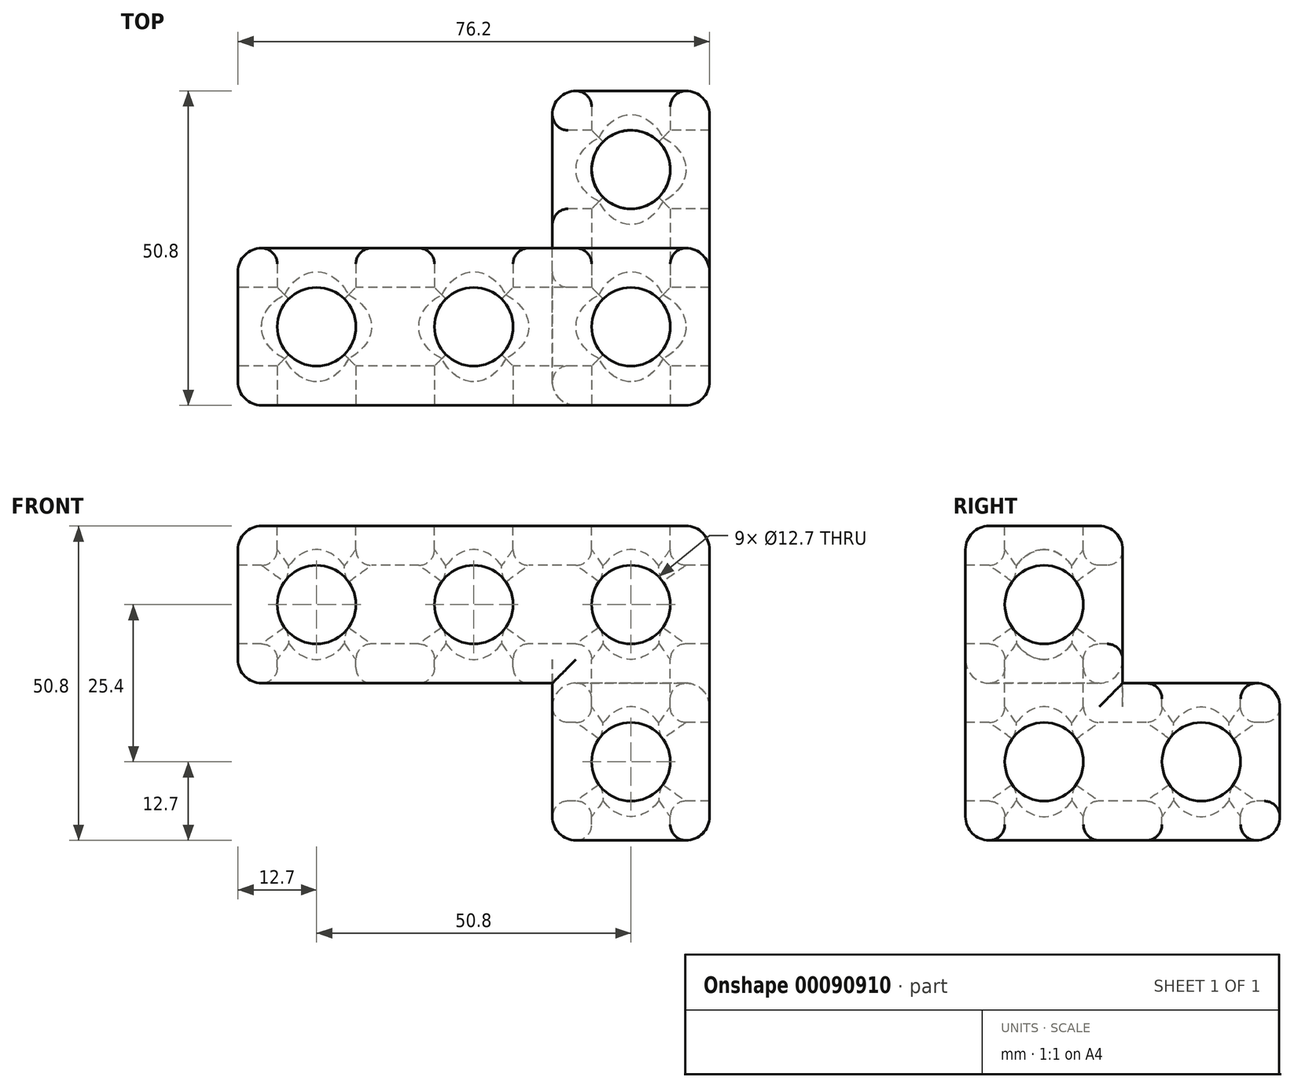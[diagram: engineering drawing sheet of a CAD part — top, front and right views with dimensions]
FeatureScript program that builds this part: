
annotation { "Feature Type Name" : "Feature", "Feature Type Description" : "" }
export const myFeature = defineFeature(function(context is Context, id is Id, definition is map)
    precondition{}
    {
        {
            var Q0;
            Q0=qCreatedBy(makeId("Top.planeOp"),FACE);
            var sketch = newSketch(context, id + "F0", { "sketchPlane" : qUnion([Q0])});
            skLineSegment(sketch, "E0.bottom", {"start": v(0, 0) * mm, "end": v(76.2, 0) * mm});
            skLineSegment(sketch, "E0.top", {"start": v(0, 25.4) * mm, "end": v(76.2, 25.4) * mm});
            skLineSegment(sketch, "E0.left", {"start": v(0, 0) * mm, "end": v(0, 25.4) * mm});
            skLineSegment(sketch, "E0.right", {"start": v(76.2, 0) * mm, "end": v(76.2, 25.4) * mm});
            skSolve(sketch);
        }
        {
            var Q0;
            Q0 = qSketchRegion(id + "F0", true);
            extrude(context, id + "F1", {"entities" : qUnion([Q0]), "depth" : 25.4 * mm});
        }
        {
            var Q0;
            Q0=makeQuery(id+"F1.opExtrude","CAP_FACE",FACE,{"disambiguationData":[OSD([sQuery(id+"F0.wireOp",EDGE,"E0.bottom"),sQuery(id+"F0.wireOp",EDGE,"E0.top"),sQuery(id+"F0.wireOp",EDGE,"E0.left"),sQuery(id+"F0.wireOp",EDGE,"E0.right")])],"isStart":true});
            var sketch = newSketch(context, id + "F2", { "sketchPlane" : qUnion([Q0])});
            skLineSegment(sketch, "E1.bottom", {"start": v(76.2, 0) * mm, "end": v(50.8, 0) * mm});
            skLineSegment(sketch, "E1.top", {"start": v(76.2, -50.8) * mm, "end": v(50.8, -50.8) * mm});
            skLineSegment(sketch, "E1.left", {"start": v(76.2, 0) * mm, "end": v(76.2, -50.8) * mm});
            skLineSegment(sketch, "E1.right", {"start": v(50.8, 0) * mm, "end": v(50.8, -50.8) * mm});
            skSolve(sketch);
        }
        {
            var Q0;
            Q0 = qSketchRegion(id + "F2", true);
            extrude(context, id + "F3", {"entities" : qUnion([Q0]), "operationType" : NewBodyOperationType.ADD, "depth" : 25.4 * mm});
        }
        {
            var Q0;
            Q0=makeQuery(id+"F1.opExtrude","CAP_FACE",FACE,{"disambiguationData":[OSD([sQuery(id+"F0.wireOp",EDGE,"E0.bottom"),sQuery(id+"F0.wireOp",EDGE,"E0.top"),sQuery(id+"F0.wireOp",EDGE,"E0.left"),sQuery(id+"F0.wireOp",EDGE,"E0.right")])],"isStart":false});
            var sketch = newSketch(context, id + "F4", { "sketchPlane" : qUnion([Q0])});
            skCircle(sketch, "E2", {"center": v(12.7, 12.7) * mm, "radius": 6.35 * mm});
            skCircle(sketch, "E3.0.1.0", {"center": v(12.7, 38.1) * mm, "radius": 6.35 * mm});
            skCircle(sketch, "E3.1.0.0", {"center": v(38.1, 12.7) * mm, "radius": 6.35 * mm});
            skCircle(sketch, "E3.1.1.0", {"center": v(38.1, 38.1) * mm, "radius": 6.35 * mm});
            skCircle(sketch, "E3.2.0.0", {"center": v(63.5, 12.7) * mm, "radius": 6.35 * mm});
            skCircle(sketch, "E3.2.1.0", {"center": v(63.5, 38.1) * mm, "radius": 6.35 * mm});
            skLineSegment(sketch, "E3.direction1", {"start": v(12.7, 12.7) * mm, "end": v(38.1, 12.7) * mm, "construction": true});
            skLineSegment(sketch, "E3.direction2", {"start": v(12.7, 12.7) * mm, "end": v(12.7, 38.1) * mm, "construction": true});
            skSolve(sketch);
        }
        {
            var Q0;
            Q0 = qSketchRegion(id + "F4", true);
            extrude(context, id + "F5", {"entities" : qUnion([Q0]), "operationType" : NewBodyOperationType.REMOVE, "oppositeDirection" : true, "depth" : 76.2 * mm});
        }
        {
            var Q0;
            Q0=makeQuery(id+"F3.boolean.opBoolean","MERGE",FACE,{"derivedFrom":[makeQuery(id+"F1.opExtrude","SWEPT_FACE",FACE,{"disambiguationData":[OSD([sQuery(id+"F0.wireOp",EDGE,"E0.bottom")])]}),makeQuery(id+"F3.opExtrude","SWEPT_FACE",FACE,{"disambiguationData":[OSD([sQuery(id+"F2.wireOp",EDGE,"E1.bottom")])]})]});
            var sketch = newSketch(context, id + "F6", { "sketchPlane" : qUnion([Q0])});
            skCircle(sketch, "E4", {"center": v(12.7, 12.7) * mm, "radius": 6.35 * mm});
            skCircle(sketch, "E5.0.1.0", {"center": v(12.7, -12.7) * mm, "radius": 6.35 * mm});
            skCircle(sketch, "E5.1.0.0", {"center": v(38.1, 12.7) * mm, "radius": 6.35 * mm});
            skCircle(sketch, "E5.1.1.0", {"center": v(38.1, -12.7) * mm, "radius": 6.35 * mm});
            skCircle(sketch, "E5.2.0.0", {"center": v(63.5, 12.7) * mm, "radius": 6.35 * mm});
            skCircle(sketch, "E5.2.1.0", {"center": v(63.5, -12.7) * mm, "radius": 6.35 * mm});
            skLineSegment(sketch, "E5.direction1", {"start": v(12.7, 12.7) * mm, "end": v(38.1, 12.7) * mm, "construction": true});
            skLineSegment(sketch, "E5.direction2", {"start": v(12.7, 12.7) * mm, "end": v(12.7, -12.7) * mm, "construction": true});
            skSolve(sketch);
        }
        {
            var Q0;
            Q0 = qSketchRegion(id + "F6", true);
            extrude(context, id + "F7", {"entities" : qUnion([Q0]), "operationType" : NewBodyOperationType.REMOVE, "oppositeDirection" : true, "depth" : 76.2 * mm});
        }
        {
            var Q0;
            Q0=makeQuery(id+"F1.opExtrude","SWEPT_FACE",FACE,{"disambiguationData":[OSD([sQuery(id+"F0.wireOp",EDGE,"E0.left")])]});
            var sketch = newSketch(context, id + "F8", { "sketchPlane" : qUnion([Q0])});
            skCircle(sketch, "E6", {"center": v(-12.7, 12.7) * mm, "radius": 6.35 * mm});
            skCircle(sketch, "E7.0.1.0", {"center": v(-12.7, -12.7) * mm, "radius": 6.35 * mm});
            skCircle(sketch, "E7.1.0.0", {"center": v(-38.1, 12.7) * mm, "radius": 6.35 * mm});
            skCircle(sketch, "E7.1.1.0", {"center": v(-38.1, -12.7) * mm, "radius": 6.35 * mm});
            skLineSegment(sketch, "E7.direction1", {"start": v(-12.7, 12.7) * mm, "end": v(-38.1, 12.7) * mm, "construction": true});
            skLineSegment(sketch, "E7.direction2", {"start": v(-12.7, 12.7) * mm, "end": v(-12.7, -12.7) * mm, "construction": true});
            skSolve(sketch);
        }
        {
            var Q0;
            Q0 = qSketchRegion(id + "F8", true);
            extrude(context, id + "F9", {"entities" : qUnion([Q0]), "operationType" : NewBodyOperationType.REMOVE, "oppositeDirection" : true, "depth" : 76.2 * mm});
        }
        {
            var Q0;
            Q0=makeQuery(id+"F5.boolean.opBoolean","COPY",EDGE,{"derivedFrom":makeQuery(id+"F5.opExtrude","CAP_EDGE",EDGE,{"disambiguationData":[OSD([sQuery(id+"F4.wireOp",EDGE,"E2")])],"isStart":true})});
            var Q1;
            Q1=makeQuery(id+"F5.boolean.opBoolean","COPY",EDGE,{"derivedFrom":makeQuery(id+"F5.opExtrude","CAP_EDGE",EDGE,{"disambiguationData":[OSD([sQuery(id+"F4.wireOp",EDGE,"E3.1.0.0")])],"isStart":true})});
            var Q2;
            Q2=makeQuery(id+"F5.boolean.opBoolean","COPY",EDGE,{"derivedFrom":makeQuery(id+"F5.opExtrude","CAP_EDGE",EDGE,{"disambiguationData":[OSD([sQuery(id+"F4.wireOp",EDGE,"E3.2.0.0")])],"isStart":true})});
            var Q3;
            Q3=makeQuery(id+"F7.boolean.opBoolean","COPY",EDGE,{"derivedFrom":makeQuery(id+"F7.opExtrude","CAP_EDGE",EDGE,{"disambiguationData":[OSD([sQuery(id+"F6.wireOp",EDGE,"E4")])],"isStart":true})});
            var Q4;
            Q4=makeQuery(id+"F5.boolean.opBoolean","INTERSECT",EDGE,{"derivedFrom":[makeQuery(id+"F3.opExtrude","CAP_FACE",FACE,{"disambiguationData":[OSD([sQuery(id+"F2.wireOp",EDGE,"E1.bottom"),sQuery(id+"F2.wireOp",EDGE,"E1.top"),sQuery(id+"F2.wireOp",EDGE,"E1.left"),sQuery(id+"F2.wireOp",EDGE,"E1.right")])],"isStart":true}),makeQuery(id+"F5.opExtrude","SWEPT_FACE",FACE,{"disambiguationData":[OSD([sQuery(id+"F4.wireOp",EDGE,"E3.2.1.0")])]})]});
            var Q5;
            Q5=makeQuery(id+"F7.boolean.opBoolean","COPY",EDGE,{"derivedFrom":makeQuery(id+"F7.opExtrude","CAP_EDGE",EDGE,{"disambiguationData":[OSD([sQuery(id+"F6.wireOp",EDGE,"E5.1.0.0")])],"isStart":true})});
            var Q6;
            Q6=makeQuery(id+"F7.boolean.opBoolean","COPY",EDGE,{"derivedFrom":makeQuery(id+"F7.opExtrude","CAP_EDGE",EDGE,{"disambiguationData":[OSD([sQuery(id+"F6.wireOp",EDGE,"E5.2.0.0")])],"isStart":true})});
            var Q7;
            Q7=makeQuery(id+"F7.boolean.opBoolean","COPY",EDGE,{"derivedFrom":makeQuery(id+"F7.opExtrude","CAP_EDGE",EDGE,{"disambiguationData":[OSD([sQuery(id+"F6.wireOp",EDGE,"E5.2.1.0")])],"isStart":true})});
            var Q8;
            Q8=makeQuery(id+"F9.boolean.opBoolean","COPY",EDGE,{"derivedFrom":makeQuery(id+"F9.opExtrude","CAP_EDGE",EDGE,{"disambiguationData":[OSD([sQuery(id+"F8.wireOp",EDGE,"E7.0.1.0")])],"isStart":false})});
            var Q9;
            Q9=makeQuery(id+"F9.boolean.opBoolean","COPY",EDGE,{"derivedFrom":makeQuery(id+"F9.opExtrude","CAP_EDGE",EDGE,{"disambiguationData":[OSD([sQuery(id+"F8.wireOp",EDGE,"E7.1.1.0")])],"isStart":false})});
            var Q10;
            Q10=makeQuery(id+"F9.boolean.opBoolean","COPY",EDGE,{"derivedFrom":makeQuery(id+"F9.opExtrude","CAP_EDGE",EDGE,{"disambiguationData":[OSD([sQuery(id+"F8.wireOp",EDGE,"E6")])],"isStart":false})});
            var Q11;
            Q11=makeQuery(id+"F7.boolean.opBoolean","INTERSECT",EDGE,{"derivedFrom":[makeQuery(id+"F3.opExtrude","SWEPT_FACE",FACE,{"disambiguationData":[OSD([sQuery(id+"F2.wireOp",EDGE,"E1.top")])]}),makeQuery(id+"F7.opExtrude","SWEPT_FACE",FACE,{"disambiguationData":[OSD([sQuery(id+"F6.wireOp",EDGE,"E5.2.1.0")])]})]});
            var Q12;
            Q12=makeQuery(id+"F7.boolean.opBoolean","INTERSECT",EDGE,{"derivedFrom":[makeQuery(id+"F1.opExtrude","SWEPT_FACE",FACE,{"disambiguationData":[OSD([sQuery(id+"F0.wireOp",EDGE,"E0.top")])]}),makeQuery(id+"F7.opExtrude","SWEPT_FACE",FACE,{"disambiguationData":[OSD([sQuery(id+"F6.wireOp",EDGE,"E5.1.0.0")])]})]});
            var Q13;
            Q13=makeQuery(id+"F7.boolean.opBoolean","INTERSECT",EDGE,{"derivedFrom":[makeQuery(id+"F1.opExtrude","SWEPT_FACE",FACE,{"disambiguationData":[OSD([sQuery(id+"F0.wireOp",EDGE,"E0.top")])]}),makeQuery(id+"F7.opExtrude","SWEPT_FACE",FACE,{"disambiguationData":[OSD([sQuery(id+"F6.wireOp",EDGE,"E4")])]})]});
            var Q14;
            Q14=makeQuery(id+"F9.boolean.opBoolean","COPY",EDGE,{"derivedFrom":makeQuery(id+"F9.opExtrude","CAP_EDGE",EDGE,{"disambiguationData":[OSD([sQuery(id+"F8.wireOp",EDGE,"E6")])],"isStart":true})});
            var Q15;
            Q15=makeQuery(id+"F9.boolean.opBoolean","INTERSECT",EDGE,{"derivedFrom":[makeQuery(id+"F3.opExtrude","SWEPT_FACE",FACE,{"disambiguationData":[OSD([sQuery(id+"F2.wireOp",EDGE,"E1.right")])]}),makeQuery(id+"F9.opExtrude","SWEPT_FACE",FACE,{"disambiguationData":[OSD([sQuery(id+"F8.wireOp",EDGE,"E7.1.1.0")])]})]});
            var Q16;
            Q16=makeQuery(id+"F9.boolean.opBoolean","INTERSECT",EDGE,{"derivedFrom":[makeQuery(id+"F3.opExtrude","SWEPT_FACE",FACE,{"disambiguationData":[OSD([sQuery(id+"F2.wireOp",EDGE,"E1.right")])]}),makeQuery(id+"F9.opExtrude","SWEPT_FACE",FACE,{"disambiguationData":[OSD([sQuery(id+"F8.wireOp",EDGE,"E7.0.1.0")])]})]});
            var Q17;
            Q17=makeQuery(id+"F5.boolean.opBoolean","INTERSECT",EDGE,{"derivedFrom":[makeQuery(id+"F1.opExtrude","CAP_FACE",FACE,{"disambiguationData":[OSD([sQuery(id+"F0.wireOp",EDGE,"E0.bottom"),sQuery(id+"F0.wireOp",EDGE,"E0.top"),sQuery(id+"F0.wireOp",EDGE,"E0.left"),sQuery(id+"F0.wireOp",EDGE,"E0.right")])],"isStart":true}),makeQuery(id+"F5.opExtrude","SWEPT_FACE",FACE,{"disambiguationData":[OSD([sQuery(id+"F4.wireOp",EDGE,"E3.1.0.0")])]})]});
            var Q18;
            Q18=makeQuery(id+"F5.boolean.opBoolean","INTERSECT",EDGE,{"derivedFrom":[makeQuery(id+"F1.opExtrude","CAP_FACE",FACE,{"disambiguationData":[OSD([sQuery(id+"F0.wireOp",EDGE,"E0.bottom"),sQuery(id+"F0.wireOp",EDGE,"E0.top"),sQuery(id+"F0.wireOp",EDGE,"E0.left"),sQuery(id+"F0.wireOp",EDGE,"E0.right")])],"isStart":true}),makeQuery(id+"F5.opExtrude","SWEPT_FACE",FACE,{"disambiguationData":[OSD([sQuery(id+"F4.wireOp",EDGE,"E2")])]})]});
            var Q19;
            Q19=makeQuery(id+"F5.boolean.opBoolean","INTERSECT",EDGE,{"derivedFrom":[makeQuery(id+"F3.opExtrude","CAP_FACE",FACE,{"disambiguationData":[OSD([sQuery(id+"F2.wireOp",EDGE,"E1.bottom"),sQuery(id+"F2.wireOp",EDGE,"E1.top"),sQuery(id+"F2.wireOp",EDGE,"E1.left"),sQuery(id+"F2.wireOp",EDGE,"E1.right")])],"isStart":false}),makeQuery(id+"F5.opExtrude","SWEPT_FACE",FACE,{"disambiguationData":[OSD([sQuery(id+"F4.wireOp",EDGE,"E3.2.0.0")])]})]});
            var Q20;
            Q20=makeQuery(id+"F7.boolean.opBoolean","INTERSECT",EDGE,{"derivedFrom":[makeQuery(id+"F1.opExtrude","SWEPT_FACE",FACE,{"disambiguationData":[OSD([sQuery(id+"F0.wireOp",EDGE,"E0.top")])]}),makeQuery(id+"F7.opExtrude","SWEPT_FACE",FACE,{"disambiguationData":[OSD([sQuery(id+"F6.wireOp",EDGE,"E5.2.0.0")])]})]});
            var Q21;
            Q21=makeQuery(id+"F5.boolean.opBoolean","INTERSECT",EDGE,{"derivedFrom":[makeQuery(id+"F3.opExtrude","CAP_FACE",FACE,{"disambiguationData":[OSD([sQuery(id+"F2.wireOp",EDGE,"E1.bottom"),sQuery(id+"F2.wireOp",EDGE,"E1.top"),sQuery(id+"F2.wireOp",EDGE,"E1.left"),sQuery(id+"F2.wireOp",EDGE,"E1.right")])],"isStart":false}),makeQuery(id+"F5.opExtrude","SWEPT_FACE",FACE,{"disambiguationData":[OSD([sQuery(id+"F4.wireOp",EDGE,"E3.2.1.0")])]})]});
            fillet(context, id + "F10", {"entities" : qUnion([Q0, Q1, Q2, Q3, Q4, Q5, Q6, Q7, Q8, Q9, Q10, Q11, Q12, Q13, Q14, Q15, Q16, Q17, Q18, Q19, Q20, Q21]), "radius" : 2.54 * mm, "tangentPropagation" : true, "allowEdgeOverflow" : false});
        }
        {
            var Q0;
            Q0=makeQuery(id+"F1.opExtrude","CAP_EDGE",EDGE,{"disambiguationData":[OSD([sQuery(id+"F0.wireOp",EDGE,"E0.left")])],"isStart":false});
            var Q1;
            Q1=makeQuery(id+"F1.opExtrude","SWEPT_EDGE",EDGE,{"disambiguationData":[OSD([sQuery(id+"F0.wireOp",EDGE,"E0.top"),sQuery(id+"F0.wireOp",EDGE,"E0.left")])]});
            var Q2;
            Q2=makeQuery(id+"F1.opExtrude","CAP_EDGE",EDGE,{"disambiguationData":[OSD([sQuery(id+"F0.wireOp",EDGE,"E0.left")])],"isStart":true});
            var Q3;
            Q3=makeQuery(id+"F1.opExtrude","SWEPT_EDGE",EDGE,{"disambiguationData":[OSD([sQuery(id+"F0.wireOp",EDGE,"E0.bottom"),sQuery(id+"F0.wireOp",EDGE,"E0.left")])]});
            var Q4;
            Q4=makeQuery(id+"F1.opExtrude","CAP_EDGE",EDGE,{"disambiguationData":[OSD([sQuery(id+"F0.wireOp",EDGE,"E0.bottom")])],"isStart":false});
            var Q5;
            Q5=makeQuery(id+"F3.boolean.opBoolean","MERGE",EDGE,{"derivedFrom":[makeQuery(id+"F1.opExtrude","SWEPT_EDGE",EDGE,{"disambiguationData":[OSD([sQuery(id+"F0.wireOp",EDGE,"E0.bottom"),sQuery(id+"F0.wireOp",EDGE,"E0.right")])]}),makeQuery(id+"F3.opExtrude","SWEPT_EDGE",EDGE,{"disambiguationData":[OSD([sQuery(id+"F2.wireOp",EDGE,"E1.bottom"),sQuery(id+"F2.wireOp",EDGE,"E1.left")])]})]});
            var Q6;
            Q6=makeQuery(id+"F3.opExtrude","SWEPT_EDGE",EDGE,{"disambiguationData":[OSD([sQuery(id+"F0.wireOp",EDGE,"E0.bottom"),sQuery(id+"F2.wireOp",EDGE,"E1.bottom"),sQuery(id+"F2.wireOp",EDGE,"E1.right")])]});
            var Q7;
            Q7=makeQuery(id+"F3.opExtrude","CAP_EDGE",EDGE,{"disambiguationData":[OSD([sQuery(id+"F2.wireOp",EDGE,"E1.bottom")])],"isStart":false});
            var Q8;
            Q8=makeQuery(id+"F3.opExtrude","CAP_EDGE",EDGE,{"disambiguationData":[OSD([sQuery(id+"F2.wireOp",EDGE,"E1.right")])],"isStart":false});
            var Q9;
            Q9=makeQuery(id+"F3.opExtrude","SWEPT_EDGE",EDGE,{"disambiguationData":[OSD([sQuery(id+"F2.wireOp",EDGE,"E1.top"),sQuery(id+"F2.wireOp",EDGE,"E1.right")])]});
            var Q10;
            {var subQ1=sQuery(id+"F2.wireOp",EDGE,"E1.top");var subQ2=sQuery(id+"F2.wireOp",EDGE,"E1.right");Q10=makeQuery(id+"F3.boolean.opBoolean","SPLIT",EDGE,{"disambiguationData":[TD([makeQuery(id+"F3.opExtrude","SWEPT_FACE",FACE,{"disambiguationData":[OSD([subQ1])]})])],"derivedFrom":makeQuery(id+"F3.opExtrude","CAP_EDGE",EDGE,{"disambiguationData":[OSD([subQ2])],"isStart":true})});}
            var Q11;
            Q11=makeQuery(id+"F1.opExtrude","CAP_EDGE",EDGE,{"disambiguationData":[OSD([sQuery(id+"F0.wireOp",EDGE,"E0.top")])],"isStart":false});
            var Q12;
            Q12=makeQuery(id+"F1.opExtrude","CAP_EDGE",EDGE,{"disambiguationData":[OSD([sQuery(id+"F0.wireOp",EDGE,"E0.right")])],"isStart":false});
            var Q13;
            Q13=makeQuery(id+"F3.opExtrude","CAP_EDGE",EDGE,{"disambiguationData":[OSD([sQuery(id+"F2.wireOp",EDGE,"E1.top")])],"isStart":true});
            var Q14;
            Q14=makeQuery(id+"F1.opExtrude","SWEPT_EDGE",EDGE,{"disambiguationData":[OSD([sQuery(id+"F0.wireOp",EDGE,"E0.top"),sQuery(id+"F0.wireOp",EDGE,"E0.right")])]});
            var Q15;
            Q15=makeQuery(id+"F3.opExtrude","CAP_EDGE",EDGE,{"disambiguationData":[OSD([sQuery(id+"F2.wireOp",EDGE,"E1.left")])],"isStart":true});
            var Q16;
            Q16=makeQuery(id+"F3.opExtrude","SWEPT_EDGE",EDGE,{"disambiguationData":[OSD([sQuery(id+"F2.wireOp",EDGE,"E1.top"),sQuery(id+"F2.wireOp",EDGE,"E1.left")])]});
            var Q17;
            Q17=makeQuery(id+"F3.opExtrude","CAP_EDGE",EDGE,{"disambiguationData":[OSD([sQuery(id+"F2.wireOp",EDGE,"E1.top")])],"isStart":false});
            var Q18;
            Q18=makeQuery(id+"F1.opExtrude","CAP_EDGE",EDGE,{"disambiguationData":[OSD([sQuery(id+"F0.wireOp",EDGE,"E0.bottom")])],"isStart":true});
            var Q19;
            Q19=makeQuery(id+"F3.opExtrude","CAP_EDGE",EDGE,{"disambiguationData":[OSD([sQuery(id+"F2.wireOp",EDGE,"E1.left")])],"isStart":false});
            fillet(context, id + "F11", {"entities" : qUnion([Q0, Q1, Q2, Q3, Q4, Q5, Q6, Q7, Q8, Q9, Q10, Q11, Q12, Q13, Q14, Q15, Q16, Q17, Q18, Q19]), "radius" : 3.8 * mm, "tangentPropagation" : true, "allowEdgeOverflow" : false});
        }
        {
            var Q0;
            {var subQ0=sQuery(id+"F0.wireOp",EDGE,"E0.left");var subQ2=sQuery(id+"F0.wireOp",EDGE,"E0.top");Q0=makeQuery(id+"F3.boolean.opBoolean","SPLIT",EDGE,{"disambiguationData":[TD([makeQuery(id+"F1.opExtrude","SWEPT_FACE",FACE,{"disambiguationData":[OSD([subQ0])]})])],"derivedFrom":makeQuery(id+"F1.opExtrude","CAP_EDGE",EDGE,{"disambiguationData":[OSD([subQ2])],"isStart":true})});}
            var Q1;
            {var subQ0=sQuery(id+"F2.wireOp",EDGE,"E1.right");var subQ1=sQuery(id+"F0.wireOp",EDGE,"E0.top");Q1=makeQuery(id+"F11.opFillet","TWEAK_EDGE",EDGE,{"derivedFrom":[makeQuery(id+"F3.boolean.opBoolean","TWEAK_VERTEX",VERTEX,{"derivedFrom":[makeQuery(id+"F1.opExtrude","CAP_FACE",FACE,{"disambiguationData":[OSD([sQuery(id+"F0.wireOp",EDGE,"E0.bottom"),subQ1,sQuery(id+"F0.wireOp",EDGE,"E0.left"),sQuery(id+"F0.wireOp",EDGE,"E0.right")])],"isStart":true}),makeQuery(id+"F1.opExtrude","SWEPT_FACE",FACE,{"disambiguationData":[OSD([subQ1])]}),makeQuery(id+"F3.opExtrude","CAP_FACE",FACE,{"disambiguationData":[OSD([sQuery(id+"F2.wireOp",EDGE,"E1.bottom"),sQuery(id+"F2.wireOp",EDGE,"E1.top"),sQuery(id+"F2.wireOp",EDGE,"E1.left"),subQ0])],"isStart":true}),makeQuery(id+"F3.opExtrude","SWEPT_FACE",FACE,{"disambiguationData":[OSD([subQ0])]})]})]});}
            fillet(context, id + "F12", {"entities" : qUnion([Q0, Q1]), "radius" : 3.8 * mm, "tangentPropagation" : true, "allowEdgeOverflow" : false});
        }
        {
            var Q0;
            {var subQ0=makeQuery(id+"F5.boolean.opBoolean","COPY",FACE,{"derivedFrom":makeQuery(id+"F5.opExtrude","SWEPT_FACE",FACE,{"disambiguationData":[OSD([sQuery(id+"F4.wireOp",EDGE,"E2")])]})});Q0=makeQuery(id+"F9.boolean.opBoolean","INTERSECT",EDGE,{"disambiguationData":[OD(0.0)],"derivedFrom":[makeQuery(id+"F7.boolean.opBoolean","SPLIT",FACE,{"disambiguationData":[TD([makeQuery(id+"F1.opExtrude","CAP_FACE",FACE,{"disambiguationData":[OSD([sQuery(id+"F0.wireOp",EDGE,"E0.bottom"),sQuery(id+"F0.wireOp",EDGE,"E0.top"),sQuery(id+"F0.wireOp",EDGE,"E0.left"),sQuery(id+"F0.wireOp",EDGE,"E0.right")])],"isStart":true})])],"derivedFrom":subQ0}),makeQuery(id+"F9.opExtrude","SWEPT_FACE",FACE,{"disambiguationData":[OSD([sQuery(id+"F8.wireOp",EDGE,"E6")])]})]});}
            var Q1;
            Q1=makeQuery(id+"F7.boolean.opBoolean","INTERSECT",EDGE,{"disambiguationData":[OD(2.0)],"derivedFrom":[makeQuery(id+"F5.boolean.opBoolean","COPY",FACE,{"derivedFrom":makeQuery(id+"F5.opExtrude","SWEPT_FACE",FACE,{"disambiguationData":[OSD([sQuery(id+"F4.wireOp",EDGE,"E2")])]})}),makeQuery(id+"F7.opExtrude","SWEPT_FACE",FACE,{"disambiguationData":[OSD([sQuery(id+"F6.wireOp",EDGE,"E4")])]})]});
            var Q2;
            Q2=makeQuery(id+"F9.boolean.opBoolean","INTERSECT",EDGE,{"disambiguationData":[OD(0.0)],"derivedFrom":[makeQuery(id+"F7.boolean.opBoolean","COPY",FACE,{"disambiguationData":[OD(0.0)],"derivedFrom":makeQuery(id+"F7.opExtrude","SWEPT_FACE",FACE,{"disambiguationData":[OSD([sQuery(id+"F6.wireOp",EDGE,"E4")])]})}),makeQuery(id+"F9.opExtrude","SWEPT_FACE",FACE,{"disambiguationData":[OSD([sQuery(id+"F8.wireOp",EDGE,"E6")])]})]});
            var Q3;
            Q3=makeQuery(id+"F9.boolean.opBoolean","INTERSECT",EDGE,{"disambiguationData":[OD(0.0)],"derivedFrom":[makeQuery(id+"F7.boolean.opBoolean","COPY",FACE,{"disambiguationData":[OD(0.0)],"derivedFrom":makeQuery(id+"F7.opExtrude","SWEPT_FACE",FACE,{"disambiguationData":[OSD([sQuery(id+"F6.wireOp",EDGE,"E5.1.0.0")])]})}),makeQuery(id+"F9.opExtrude","SWEPT_FACE",FACE,{"disambiguationData":[OSD([sQuery(id+"F8.wireOp",EDGE,"E6")])]})]});
            var Q4;
            {var subQ0=makeQuery(id+"F5.boolean.opBoolean","COPY",FACE,{"derivedFrom":makeQuery(id+"F5.opExtrude","SWEPT_FACE",FACE,{"disambiguationData":[OSD([sQuery(id+"F4.wireOp",EDGE,"E3.1.0.0")])]})});Q4=makeQuery(id+"F9.boolean.opBoolean","INTERSECT",EDGE,{"disambiguationData":[OD(0.0)],"derivedFrom":[makeQuery(id+"F7.boolean.opBoolean","SPLIT",FACE,{"disambiguationData":[TD([makeQuery(id+"F1.opExtrude","CAP_FACE",FACE,{"disambiguationData":[OSD([sQuery(id+"F0.wireOp",EDGE,"E0.bottom"),sQuery(id+"F0.wireOp",EDGE,"E0.top"),sQuery(id+"F0.wireOp",EDGE,"E0.left"),sQuery(id+"F0.wireOp",EDGE,"E0.right")])],"isStart":true})])],"derivedFrom":subQ0}),makeQuery(id+"F9.opExtrude","SWEPT_FACE",FACE,{"disambiguationData":[OSD([sQuery(id+"F8.wireOp",EDGE,"E6")])]})]});}
            var Q5;
            Q5=makeQuery(id+"F7.boolean.opBoolean","INTERSECT",EDGE,{"disambiguationData":[OD(2.0)],"derivedFrom":[makeQuery(id+"F5.boolean.opBoolean","COPY",FACE,{"derivedFrom":makeQuery(id+"F5.opExtrude","SWEPT_FACE",FACE,{"disambiguationData":[OSD([sQuery(id+"F4.wireOp",EDGE,"E3.1.0.0")])]})}),makeQuery(id+"F7.opExtrude","SWEPT_FACE",FACE,{"disambiguationData":[OSD([sQuery(id+"F6.wireOp",EDGE,"E5.1.0.0")])]})]});
            var Q6;
            Q6=makeQuery(id+"F9.boolean.opBoolean","INTERSECT",EDGE,{"disambiguationData":[OD(1.0)],"derivedFrom":[makeQuery(id+"F7.boolean.opBoolean","COPY",FACE,{"disambiguationData":[OD(0.0)],"derivedFrom":makeQuery(id+"F7.opExtrude","SWEPT_FACE",FACE,{"disambiguationData":[OSD([sQuery(id+"F6.wireOp",EDGE,"E5.2.0.0")])]})}),makeQuery(id+"F9.opExtrude","SWEPT_FACE",FACE,{"disambiguationData":[OSD([sQuery(id+"F8.wireOp",EDGE,"E6")])]})]});
            var Q7;
            {var subQ0=makeQuery(id+"F5.boolean.opBoolean","COPY",FACE,{"derivedFrom":makeQuery(id+"F5.opExtrude","SWEPT_FACE",FACE,{"disambiguationData":[OSD([sQuery(id+"F4.wireOp",EDGE,"E3.2.0.0")])]})});Q7=makeQuery(id+"F9.boolean.opBoolean","INTERSECT",EDGE,{"disambiguationData":[OD(1.0)],"derivedFrom":[makeQuery(id+"F7.boolean.opBoolean","SPLIT",FACE,{"disambiguationData":[TD([subQ0,makeQuery(id+"F7.opExtrude","SWEPT_FACE",FACE,{"disambiguationData":[OSD([sQuery(id+"F6.wireOp",EDGE,"E5.2.0.0")])]}),makeQuery(id+"F7.opExtrude","SWEPT_FACE",FACE,{"disambiguationData":[OSD([sQuery(id+"F6.wireOp",EDGE,"E5.2.1.0")])]})])],"derivedFrom":subQ0}),makeQuery(id+"F9.opExtrude","SWEPT_FACE",FACE,{"disambiguationData":[OSD([sQuery(id+"F8.wireOp",EDGE,"E6")])]})]});}
            var Q8;
            Q8=makeQuery(id+"F7.boolean.opBoolean","INTERSECT",EDGE,{"disambiguationData":[OD(2.0)],"derivedFrom":[makeQuery(id+"F5.boolean.opBoolean","COPY",FACE,{"derivedFrom":makeQuery(id+"F5.opExtrude","SWEPT_FACE",FACE,{"disambiguationData":[OSD([sQuery(id+"F4.wireOp",EDGE,"E3.2.0.0")])]})}),makeQuery(id+"F7.opExtrude","SWEPT_FACE",FACE,{"disambiguationData":[OSD([sQuery(id+"F6.wireOp",EDGE,"E5.2.0.0")])]})]});
            var Q9;
            {var subQ0=makeQuery(id+"F5.boolean.opBoolean","COPY",FACE,{"derivedFrom":makeQuery(id+"F5.opExtrude","SWEPT_FACE",FACE,{"disambiguationData":[OSD([sQuery(id+"F4.wireOp",EDGE,"E3.2.0.0")])]})});Q9=makeQuery(id+"F9.boolean.opBoolean","INTERSECT",EDGE,{"disambiguationData":[OD(1.0)],"derivedFrom":[makeQuery(id+"F7.boolean.opBoolean","SPLIT",FACE,{"disambiguationData":[TD([makeQuery(id+"F3.opExtrude","CAP_FACE",FACE,{"disambiguationData":[OSD([sQuery(id+"F2.wireOp",EDGE,"E1.bottom"),sQuery(id+"F2.wireOp",EDGE,"E1.top"),sQuery(id+"F2.wireOp",EDGE,"E1.left"),sQuery(id+"F2.wireOp",EDGE,"E1.right")])],"isStart":false}),subQ0,makeQuery(id+"F7.opExtrude","SWEPT_FACE",FACE,{"disambiguationData":[OSD([sQuery(id+"F6.wireOp",EDGE,"E5.2.1.0")])]})])],"derivedFrom":subQ0}),makeQuery(id+"F9.opExtrude","SWEPT_FACE",FACE,{"disambiguationData":[OSD([sQuery(id+"F8.wireOp",EDGE,"E7.0.1.0")])]})]});}
            var Q10;
            Q10=makeQuery(id+"F9.boolean.opBoolean","INTERSECT",EDGE,{"disambiguationData":[OD(1.0)],"derivedFrom":[makeQuery(id+"F7.boolean.opBoolean","COPY",FACE,{"disambiguationData":[OD(0.0)],"derivedFrom":makeQuery(id+"F7.opExtrude","SWEPT_FACE",FACE,{"disambiguationData":[OSD([sQuery(id+"F6.wireOp",EDGE,"E5.2.1.0")])]})}),makeQuery(id+"F9.opExtrude","SWEPT_FACE",FACE,{"disambiguationData":[OSD([sQuery(id+"F8.wireOp",EDGE,"E7.0.1.0")])]})]});
            var Q11;
            Q11=makeQuery(id+"F7.boolean.opBoolean","INTERSECT",EDGE,{"disambiguationData":[OD(0.0)],"derivedFrom":[makeQuery(id+"F5.boolean.opBoolean","COPY",FACE,{"derivedFrom":makeQuery(id+"F5.opExtrude","SWEPT_FACE",FACE,{"disambiguationData":[OSD([sQuery(id+"F4.wireOp",EDGE,"E3.2.0.0")])]})}),makeQuery(id+"F7.opExtrude","SWEPT_FACE",FACE,{"disambiguationData":[OSD([sQuery(id+"F6.wireOp",EDGE,"E5.2.1.0")])]})]});
            var Q12;
            Q12=makeQuery(id+"F7.boolean.opBoolean","INTERSECT",EDGE,{"disambiguationData":[OD(1.0)],"derivedFrom":[makeQuery(id+"F5.boolean.opBoolean","COPY",FACE,{"derivedFrom":makeQuery(id+"F5.opExtrude","SWEPT_FACE",FACE,{"disambiguationData":[OSD([sQuery(id+"F4.wireOp",EDGE,"E2")])]})}),makeQuery(id+"F7.opExtrude","SWEPT_FACE",FACE,{"disambiguationData":[OSD([sQuery(id+"F6.wireOp",EDGE,"E4")])]})]});
            var Q13;
            Q13=makeQuery(id+"F7.boolean.opBoolean","INTERSECT",EDGE,{"disambiguationData":[OD(1.0)],"derivedFrom":[makeQuery(id+"F5.boolean.opBoolean","COPY",FACE,{"derivedFrom":makeQuery(id+"F5.opExtrude","SWEPT_FACE",FACE,{"disambiguationData":[OSD([sQuery(id+"F4.wireOp",EDGE,"E3.1.0.0")])]})}),makeQuery(id+"F7.opExtrude","SWEPT_FACE",FACE,{"disambiguationData":[OSD([sQuery(id+"F6.wireOp",EDGE,"E5.1.0.0")])]})]});
            var Q14;
            Q14=makeQuery(id+"F7.boolean.opBoolean","INTERSECT",EDGE,{"disambiguationData":[OD(1.0)],"derivedFrom":[makeQuery(id+"F5.boolean.opBoolean","COPY",FACE,{"derivedFrom":makeQuery(id+"F5.opExtrude","SWEPT_FACE",FACE,{"disambiguationData":[OSD([sQuery(id+"F4.wireOp",EDGE,"E3.2.0.0")])]})}),makeQuery(id+"F7.opExtrude","SWEPT_FACE",FACE,{"disambiguationData":[OSD([sQuery(id+"F6.wireOp",EDGE,"E5.2.0.0")])]})]});
            var Q15;
            Q15=makeQuery(id+"F7.boolean.opBoolean","INTERSECT",EDGE,{"disambiguationData":[OD(3.0)],"derivedFrom":[makeQuery(id+"F5.boolean.opBoolean","COPY",FACE,{"derivedFrom":makeQuery(id+"F5.opExtrude","SWEPT_FACE",FACE,{"disambiguationData":[OSD([sQuery(id+"F4.wireOp",EDGE,"E3.2.0.0")])]})}),makeQuery(id+"F7.opExtrude","SWEPT_FACE",FACE,{"disambiguationData":[OSD([sQuery(id+"F6.wireOp",EDGE,"E5.2.0.0")])]})]});
            var Q16;
            Q16=makeQuery(id+"F9.boolean.opBoolean","INTERSECT",EDGE,{"disambiguationData":[OD(1.0)],"derivedFrom":[makeQuery(id+"F7.boolean.opBoolean","COPY",FACE,{"disambiguationData":[OD(1.0)],"derivedFrom":makeQuery(id+"F7.opExtrude","SWEPT_FACE",FACE,{"disambiguationData":[OSD([sQuery(id+"F6.wireOp",EDGE,"E5.2.0.0")])]})}),makeQuery(id+"F9.opExtrude","SWEPT_FACE",FACE,{"disambiguationData":[OSD([sQuery(id+"F8.wireOp",EDGE,"E6")])]})]});
            var Q17;
            {var subQ0=makeQuery(id+"F5.boolean.opBoolean","COPY",FACE,{"derivedFrom":makeQuery(id+"F5.opExtrude","SWEPT_FACE",FACE,{"disambiguationData":[OSD([sQuery(id+"F4.wireOp",EDGE,"E3.2.0.0")])]})});Q17=makeQuery(id+"F9.boolean.opBoolean","INTERSECT",EDGE,{"disambiguationData":[OD(1.0)],"derivedFrom":[makeQuery(id+"F7.boolean.opBoolean","SPLIT",FACE,{"disambiguationData":[TD([makeQuery(id+"F1.opExtrude","CAP_FACE",FACE,{"disambiguationData":[OSD([sQuery(id+"F0.wireOp",EDGE,"E0.bottom"),sQuery(id+"F0.wireOp",EDGE,"E0.top"),sQuery(id+"F0.wireOp",EDGE,"E0.left"),sQuery(id+"F0.wireOp",EDGE,"E0.right")])],"isStart":false}),subQ0,makeQuery(id+"F7.opExtrude","SWEPT_FACE",FACE,{"disambiguationData":[OSD([sQuery(id+"F6.wireOp",EDGE,"E5.2.0.0")])]})])],"derivedFrom":subQ0}),makeQuery(id+"F9.opExtrude","SWEPT_FACE",FACE,{"disambiguationData":[OSD([sQuery(id+"F8.wireOp",EDGE,"E6")])]})]});}
            var Q18;
            {var subQ0=makeQuery(id+"F5.boolean.opBoolean","COPY",FACE,{"derivedFrom":makeQuery(id+"F5.opExtrude","SWEPT_FACE",FACE,{"disambiguationData":[OSD([sQuery(id+"F4.wireOp",EDGE,"E3.1.0.0")])]})});Q18=makeQuery(id+"F9.boolean.opBoolean","INTERSECT",EDGE,{"disambiguationData":[OD(0.0)],"derivedFrom":[makeQuery(id+"F7.boolean.opBoolean","SPLIT",FACE,{"disambiguationData":[TD([makeQuery(id+"F1.opExtrude","CAP_FACE",FACE,{"disambiguationData":[OSD([sQuery(id+"F0.wireOp",EDGE,"E0.bottom"),sQuery(id+"F0.wireOp",EDGE,"E0.top"),sQuery(id+"F0.wireOp",EDGE,"E0.left"),sQuery(id+"F0.wireOp",EDGE,"E0.right")])],"isStart":false})])],"derivedFrom":subQ0}),makeQuery(id+"F9.opExtrude","SWEPT_FACE",FACE,{"disambiguationData":[OSD([sQuery(id+"F8.wireOp",EDGE,"E6")])]})]});}
            var Q19;
            Q19=makeQuery(id+"F9.boolean.opBoolean","INTERSECT",EDGE,{"disambiguationData":[OD(0.0)],"derivedFrom":[makeQuery(id+"F7.boolean.opBoolean","COPY",FACE,{"disambiguationData":[OD(1.0)],"derivedFrom":makeQuery(id+"F7.opExtrude","SWEPT_FACE",FACE,{"disambiguationData":[OSD([sQuery(id+"F6.wireOp",EDGE,"E5.1.0.0")])]})}),makeQuery(id+"F9.opExtrude","SWEPT_FACE",FACE,{"disambiguationData":[OSD([sQuery(id+"F8.wireOp",EDGE,"E6")])]})]});
            var Q20;
            Q20=makeQuery(id+"F7.boolean.opBoolean","INTERSECT",EDGE,{"disambiguationData":[OD(3.0)],"derivedFrom":[makeQuery(id+"F5.boolean.opBoolean","COPY",FACE,{"derivedFrom":makeQuery(id+"F5.opExtrude","SWEPT_FACE",FACE,{"disambiguationData":[OSD([sQuery(id+"F4.wireOp",EDGE,"E3.1.0.0")])]})}),makeQuery(id+"F7.opExtrude","SWEPT_FACE",FACE,{"disambiguationData":[OSD([sQuery(id+"F6.wireOp",EDGE,"E5.1.0.0")])]})]});
            var Q21;
            Q21=makeQuery(id+"F9.boolean.opBoolean","INTERSECT",EDGE,{"disambiguationData":[OD(0.0)],"derivedFrom":[makeQuery(id+"F7.boolean.opBoolean","COPY",FACE,{"disambiguationData":[OD(1.0)],"derivedFrom":makeQuery(id+"F7.opExtrude","SWEPT_FACE",FACE,{"disambiguationData":[OSD([sQuery(id+"F6.wireOp",EDGE,"E4")])]})}),makeQuery(id+"F9.opExtrude","SWEPT_FACE",FACE,{"disambiguationData":[OSD([sQuery(id+"F8.wireOp",EDGE,"E6")])]})]});
            var Q22;
            {var subQ0=makeQuery(id+"F5.boolean.opBoolean","COPY",FACE,{"derivedFrom":makeQuery(id+"F5.opExtrude","SWEPT_FACE",FACE,{"disambiguationData":[OSD([sQuery(id+"F4.wireOp",EDGE,"E2")])]})});Q22=makeQuery(id+"F9.boolean.opBoolean","INTERSECT",EDGE,{"disambiguationData":[OD(0.0)],"derivedFrom":[makeQuery(id+"F7.boolean.opBoolean","SPLIT",FACE,{"disambiguationData":[TD([makeQuery(id+"F1.opExtrude","CAP_FACE",FACE,{"disambiguationData":[OSD([sQuery(id+"F0.wireOp",EDGE,"E0.bottom"),sQuery(id+"F0.wireOp",EDGE,"E0.top"),sQuery(id+"F0.wireOp",EDGE,"E0.left"),sQuery(id+"F0.wireOp",EDGE,"E0.right")])],"isStart":false})])],"derivedFrom":subQ0}),makeQuery(id+"F9.opExtrude","SWEPT_FACE",FACE,{"disambiguationData":[OSD([sQuery(id+"F8.wireOp",EDGE,"E6")])]})]});}
            var Q23;
            Q23=makeQuery(id+"F7.boolean.opBoolean","INTERSECT",EDGE,{"disambiguationData":[OD(3.0)],"derivedFrom":[makeQuery(id+"F5.boolean.opBoolean","COPY",FACE,{"derivedFrom":makeQuery(id+"F5.opExtrude","SWEPT_FACE",FACE,{"disambiguationData":[OSD([sQuery(id+"F4.wireOp",EDGE,"E2")])]})}),makeQuery(id+"F7.opExtrude","SWEPT_FACE",FACE,{"disambiguationData":[OSD([sQuery(id+"F6.wireOp",EDGE,"E4")])]})]});
            var Q24;
            Q24=makeQuery(id+"F7.boolean.opBoolean","INTERSECT",EDGE,{"disambiguationData":[OD(0.0)],"derivedFrom":[makeQuery(id+"F5.boolean.opBoolean","COPY",FACE,{"derivedFrom":makeQuery(id+"F5.opExtrude","SWEPT_FACE",FACE,{"disambiguationData":[OSD([sQuery(id+"F4.wireOp",EDGE,"E3.2.0.0")])]})}),makeQuery(id+"F7.opExtrude","SWEPT_FACE",FACE,{"disambiguationData":[OSD([sQuery(id+"F6.wireOp",EDGE,"E5.2.0.0")])]})]});
            var Q25;
            {var subQ0=makeQuery(id+"F5.boolean.opBoolean","COPY",FACE,{"derivedFrom":makeQuery(id+"F5.opExtrude","SWEPT_FACE",FACE,{"disambiguationData":[OSD([sQuery(id+"F4.wireOp",EDGE,"E3.2.0.0")])]})});Q25=makeQuery(id+"F9.boolean.opBoolean","INTERSECT",EDGE,{"disambiguationData":[OD(0.0)],"derivedFrom":[makeQuery(id+"F7.boolean.opBoolean","SPLIT",FACE,{"disambiguationData":[TD([makeQuery(id+"F1.opExtrude","CAP_FACE",FACE,{"disambiguationData":[OSD([sQuery(id+"F0.wireOp",EDGE,"E0.bottom"),sQuery(id+"F0.wireOp",EDGE,"E0.top"),sQuery(id+"F0.wireOp",EDGE,"E0.left"),sQuery(id+"F0.wireOp",EDGE,"E0.right")])],"isStart":false}),subQ0,makeQuery(id+"F7.opExtrude","SWEPT_FACE",FACE,{"disambiguationData":[OSD([sQuery(id+"F6.wireOp",EDGE,"E5.2.0.0")])]})])],"derivedFrom":subQ0}),makeQuery(id+"F9.opExtrude","SWEPT_FACE",FACE,{"disambiguationData":[OSD([sQuery(id+"F8.wireOp",EDGE,"E6")])]})]});}
            var Q26;
            Q26=makeQuery(id+"F9.boolean.opBoolean","INTERSECT",EDGE,{"disambiguationData":[OD(0.0)],"derivedFrom":[makeQuery(id+"F7.boolean.opBoolean","COPY",FACE,{"disambiguationData":[OD(0.0)],"derivedFrom":makeQuery(id+"F7.opExtrude","SWEPT_FACE",FACE,{"disambiguationData":[OSD([sQuery(id+"F6.wireOp",EDGE,"E5.2.0.0")])]})}),makeQuery(id+"F9.opExtrude","SWEPT_FACE",FACE,{"disambiguationData":[OSD([sQuery(id+"F8.wireOp",EDGE,"E6")])]})]});
            var Q27;
            {var subQ0=makeQuery(id+"F5.boolean.opBoolean","COPY",FACE,{"derivedFrom":makeQuery(id+"F5.opExtrude","SWEPT_FACE",FACE,{"disambiguationData":[OSD([sQuery(id+"F4.wireOp",EDGE,"E3.2.0.0")])]})});Q27=makeQuery(id+"F9.boolean.opBoolean","INTERSECT",EDGE,{"disambiguationData":[OD(0.0)],"derivedFrom":[makeQuery(id+"F7.boolean.opBoolean","SPLIT",FACE,{"disambiguationData":[TD([subQ0,makeQuery(id+"F7.opExtrude","SWEPT_FACE",FACE,{"disambiguationData":[OSD([sQuery(id+"F6.wireOp",EDGE,"E5.2.0.0")])]}),makeQuery(id+"F7.opExtrude","SWEPT_FACE",FACE,{"disambiguationData":[OSD([sQuery(id+"F6.wireOp",EDGE,"E5.2.1.0")])]})])],"derivedFrom":subQ0}),makeQuery(id+"F9.opExtrude","SWEPT_FACE",FACE,{"disambiguationData":[OSD([sQuery(id+"F8.wireOp",EDGE,"E6")])]})]});}
            var Q28;
            Q28=makeQuery(id+"F9.boolean.opBoolean","INTERSECT",EDGE,{"disambiguationData":[OD(0.0)],"derivedFrom":[makeQuery(id+"F7.boolean.opBoolean","COPY",FACE,{"disambiguationData":[OD(1.0)],"derivedFrom":makeQuery(id+"F7.opExtrude","SWEPT_FACE",FACE,{"disambiguationData":[OSD([sQuery(id+"F6.wireOp",EDGE,"E5.2.0.0")])]})}),makeQuery(id+"F9.opExtrude","SWEPT_FACE",FACE,{"disambiguationData":[OSD([sQuery(id+"F8.wireOp",EDGE,"E6")])]})]});
            var Q29;
            Q29=makeQuery(id+"F9.boolean.opBoolean","INTERSECT",EDGE,{"disambiguationData":[OD(1.0)],"derivedFrom":[makeQuery(id+"F7.boolean.opBoolean","COPY",FACE,{"disambiguationData":[OD(0.0)],"derivedFrom":makeQuery(id+"F7.opExtrude","SWEPT_FACE",FACE,{"disambiguationData":[OSD([sQuery(id+"F6.wireOp",EDGE,"E5.1.0.0")])]})}),makeQuery(id+"F9.opExtrude","SWEPT_FACE",FACE,{"disambiguationData":[OSD([sQuery(id+"F8.wireOp",EDGE,"E6")])]})]});
            var Q30;
            Q30=makeQuery(id+"F9.boolean.opBoolean","INTERSECT",EDGE,{"disambiguationData":[OD(1.0)],"derivedFrom":[makeQuery(id+"F7.boolean.opBoolean","COPY",FACE,{"disambiguationData":[OD(1.0)],"derivedFrom":makeQuery(id+"F7.opExtrude","SWEPT_FACE",FACE,{"disambiguationData":[OSD([sQuery(id+"F6.wireOp",EDGE,"E5.1.0.0")])]})}),makeQuery(id+"F9.opExtrude","SWEPT_FACE",FACE,{"disambiguationData":[OSD([sQuery(id+"F8.wireOp",EDGE,"E6")])]})]});
            var Q31;
            {var subQ0=makeQuery(id+"F5.boolean.opBoolean","COPY",FACE,{"derivedFrom":makeQuery(id+"F5.opExtrude","SWEPT_FACE",FACE,{"disambiguationData":[OSD([sQuery(id+"F4.wireOp",EDGE,"E3.1.0.0")])]})});Q31=makeQuery(id+"F9.boolean.opBoolean","INTERSECT",EDGE,{"disambiguationData":[OD(1.0)],"derivedFrom":[makeQuery(id+"F7.boolean.opBoolean","SPLIT",FACE,{"disambiguationData":[TD([makeQuery(id+"F1.opExtrude","CAP_FACE",FACE,{"disambiguationData":[OSD([sQuery(id+"F0.wireOp",EDGE,"E0.bottom"),sQuery(id+"F0.wireOp",EDGE,"E0.top"),sQuery(id+"F0.wireOp",EDGE,"E0.left"),sQuery(id+"F0.wireOp",EDGE,"E0.right")])],"isStart":true})])],"derivedFrom":subQ0}),makeQuery(id+"F9.opExtrude","SWEPT_FACE",FACE,{"disambiguationData":[OSD([sQuery(id+"F8.wireOp",EDGE,"E6")])]})]});}
            var Q32;
            {var subQ0=makeQuery(id+"F5.boolean.opBoolean","COPY",FACE,{"derivedFrom":makeQuery(id+"F5.opExtrude","SWEPT_FACE",FACE,{"disambiguationData":[OSD([sQuery(id+"F4.wireOp",EDGE,"E3.1.0.0")])]})});Q32=makeQuery(id+"F9.boolean.opBoolean","INTERSECT",EDGE,{"disambiguationData":[OD(1.0)],"derivedFrom":[makeQuery(id+"F7.boolean.opBoolean","SPLIT",FACE,{"disambiguationData":[TD([makeQuery(id+"F1.opExtrude","CAP_FACE",FACE,{"disambiguationData":[OSD([sQuery(id+"F0.wireOp",EDGE,"E0.bottom"),sQuery(id+"F0.wireOp",EDGE,"E0.top"),sQuery(id+"F0.wireOp",EDGE,"E0.left"),sQuery(id+"F0.wireOp",EDGE,"E0.right")])],"isStart":false})])],"derivedFrom":subQ0}),makeQuery(id+"F9.opExtrude","SWEPT_FACE",FACE,{"disambiguationData":[OSD([sQuery(id+"F8.wireOp",EDGE,"E6")])]})]});}
            var Q33;
            Q33=makeQuery(id+"F7.boolean.opBoolean","INTERSECT",EDGE,{"disambiguationData":[OD(0.0)],"derivedFrom":[makeQuery(id+"F5.boolean.opBoolean","COPY",FACE,{"derivedFrom":makeQuery(id+"F5.opExtrude","SWEPT_FACE",FACE,{"disambiguationData":[OSD([sQuery(id+"F4.wireOp",EDGE,"E3.1.0.0")])]})}),makeQuery(id+"F7.opExtrude","SWEPT_FACE",FACE,{"disambiguationData":[OSD([sQuery(id+"F6.wireOp",EDGE,"E5.1.0.0")])]})]});
            var Q34;
            {var subQ0=makeQuery(id+"F5.boolean.opBoolean","COPY",FACE,{"derivedFrom":makeQuery(id+"F5.opExtrude","SWEPT_FACE",FACE,{"disambiguationData":[OSD([sQuery(id+"F4.wireOp",EDGE,"E2")])]})});Q34=makeQuery(id+"F9.boolean.opBoolean","INTERSECT",EDGE,{"disambiguationData":[OD(1.0)],"derivedFrom":[makeQuery(id+"F7.boolean.opBoolean","SPLIT",FACE,{"disambiguationData":[TD([makeQuery(id+"F1.opExtrude","CAP_FACE",FACE,{"disambiguationData":[OSD([sQuery(id+"F0.wireOp",EDGE,"E0.bottom"),sQuery(id+"F0.wireOp",EDGE,"E0.top"),sQuery(id+"F0.wireOp",EDGE,"E0.left"),sQuery(id+"F0.wireOp",EDGE,"E0.right")])],"isStart":false})])],"derivedFrom":subQ0}),makeQuery(id+"F9.opExtrude","SWEPT_FACE",FACE,{"disambiguationData":[OSD([sQuery(id+"F8.wireOp",EDGE,"E6")])]})]});}
            var Q35;
            Q35=makeQuery(id+"F7.boolean.opBoolean","INTERSECT",EDGE,{"disambiguationData":[OD(0.0)],"derivedFrom":[makeQuery(id+"F5.boolean.opBoolean","COPY",FACE,{"derivedFrom":makeQuery(id+"F5.opExtrude","SWEPT_FACE",FACE,{"disambiguationData":[OSD([sQuery(id+"F4.wireOp",EDGE,"E2")])]})}),makeQuery(id+"F7.opExtrude","SWEPT_FACE",FACE,{"disambiguationData":[OSD([sQuery(id+"F6.wireOp",EDGE,"E4")])]})]});
            var Q36;
            Q36=makeQuery(id+"F9.boolean.opBoolean","INTERSECT",EDGE,{"disambiguationData":[OD(1.0)],"derivedFrom":[makeQuery(id+"F7.boolean.opBoolean","COPY",FACE,{"disambiguationData":[OD(0.0)],"derivedFrom":makeQuery(id+"F7.opExtrude","SWEPT_FACE",FACE,{"disambiguationData":[OSD([sQuery(id+"F6.wireOp",EDGE,"E4")])]})}),makeQuery(id+"F9.opExtrude","SWEPT_FACE",FACE,{"disambiguationData":[OSD([sQuery(id+"F8.wireOp",EDGE,"E6")])]})]});
            var Q37;
            Q37=makeQuery(id+"F9.boolean.opBoolean","INTERSECT",EDGE,{"disambiguationData":[OD(1.0)],"derivedFrom":[makeQuery(id+"F7.boolean.opBoolean","COPY",FACE,{"disambiguationData":[OD(1.0)],"derivedFrom":makeQuery(id+"F7.opExtrude","SWEPT_FACE",FACE,{"disambiguationData":[OSD([sQuery(id+"F6.wireOp",EDGE,"E4")])]})}),makeQuery(id+"F9.opExtrude","SWEPT_FACE",FACE,{"disambiguationData":[OSD([sQuery(id+"F8.wireOp",EDGE,"E6")])]})]});
            var Q38;
            {var subQ0=makeQuery(id+"F5.boolean.opBoolean","COPY",FACE,{"derivedFrom":makeQuery(id+"F5.opExtrude","SWEPT_FACE",FACE,{"disambiguationData":[OSD([sQuery(id+"F4.wireOp",EDGE,"E2")])]})});Q38=makeQuery(id+"F9.boolean.opBoolean","INTERSECT",EDGE,{"disambiguationData":[OD(1.0)],"derivedFrom":[makeQuery(id+"F7.boolean.opBoolean","SPLIT",FACE,{"disambiguationData":[TD([makeQuery(id+"F1.opExtrude","CAP_FACE",FACE,{"disambiguationData":[OSD([sQuery(id+"F0.wireOp",EDGE,"E0.bottom"),sQuery(id+"F0.wireOp",EDGE,"E0.top"),sQuery(id+"F0.wireOp",EDGE,"E0.left"),sQuery(id+"F0.wireOp",EDGE,"E0.right")])],"isStart":true})])],"derivedFrom":subQ0}),makeQuery(id+"F9.opExtrude","SWEPT_FACE",FACE,{"disambiguationData":[OSD([sQuery(id+"F8.wireOp",EDGE,"E6")])]})]});}
            var Q39;
            Q39=makeQuery(id+"F7.boolean.opBoolean","INTERSECT",EDGE,{"disambiguationData":[OD(1.0)],"derivedFrom":[makeQuery(id+"F5.boolean.opBoolean","COPY",FACE,{"derivedFrom":makeQuery(id+"F5.opExtrude","SWEPT_FACE",FACE,{"disambiguationData":[OSD([sQuery(id+"F4.wireOp",EDGE,"E3.2.1.0")])]})}),makeQuery(id+"F7.opExtrude","SWEPT_FACE",FACE,{"disambiguationData":[OSD([sQuery(id+"F6.wireOp",EDGE,"E5.2.1.0")])]})]});
            var Q40;
            {var subQ0=makeQuery(id+"F5.boolean.opBoolean","COPY",FACE,{"derivedFrom":makeQuery(id+"F5.opExtrude","SWEPT_FACE",FACE,{"disambiguationData":[OSD([sQuery(id+"F4.wireOp",EDGE,"E3.2.1.0")])]})});Q40=makeQuery(id+"F9.boolean.opBoolean","INTERSECT",EDGE,{"disambiguationData":[OD(0.0)],"derivedFrom":[makeQuery(id+"F7.boolean.opBoolean","SPLIT",FACE,{"disambiguationData":[TD([makeQuery(id+"F3.opExtrude","CAP_FACE",FACE,{"disambiguationData":[OSD([sQuery(id+"F2.wireOp",EDGE,"E1.bottom"),sQuery(id+"F2.wireOp",EDGE,"E1.top"),sQuery(id+"F2.wireOp",EDGE,"E1.left"),sQuery(id+"F2.wireOp",EDGE,"E1.right")])],"isStart":false})])],"derivedFrom":subQ0}),makeQuery(id+"F9.opExtrude","SWEPT_FACE",FACE,{"disambiguationData":[OSD([sQuery(id+"F8.wireOp",EDGE,"E7.1.1.0")])]})]});}
            var Q41;
            Q41=makeQuery(id+"F9.boolean.opBoolean","INTERSECT",EDGE,{"disambiguationData":[OD(0.0)],"derivedFrom":[makeQuery(id+"F7.boolean.opBoolean","COPY",FACE,{"disambiguationData":[OD(2.0)],"derivedFrom":makeQuery(id+"F7.opExtrude","SWEPT_FACE",FACE,{"disambiguationData":[OSD([sQuery(id+"F6.wireOp",EDGE,"E5.2.1.0")])]})}),makeQuery(id+"F9.opExtrude","SWEPT_FACE",FACE,{"disambiguationData":[OSD([sQuery(id+"F8.wireOp",EDGE,"E7.1.1.0")])]})]});
            var Q42;
            Q42=makeQuery(id+"F7.boolean.opBoolean","INTERSECT",EDGE,{"disambiguationData":[OD(3.0)],"derivedFrom":[makeQuery(id+"F5.boolean.opBoolean","COPY",FACE,{"derivedFrom":makeQuery(id+"F5.opExtrude","SWEPT_FACE",FACE,{"disambiguationData":[OSD([sQuery(id+"F4.wireOp",EDGE,"E3.2.1.0")])]})}),makeQuery(id+"F7.opExtrude","SWEPT_FACE",FACE,{"disambiguationData":[OSD([sQuery(id+"F6.wireOp",EDGE,"E5.2.1.0")])]})]});
            var Q43;
            {var subQ0=makeQuery(id+"F5.boolean.opBoolean","COPY",FACE,{"derivedFrom":makeQuery(id+"F5.opExtrude","SWEPT_FACE",FACE,{"disambiguationData":[OSD([sQuery(id+"F4.wireOp",EDGE,"E3.2.1.0")])]})});Q43=makeQuery(id+"F9.boolean.opBoolean","INTERSECT",EDGE,{"disambiguationData":[OD(0.0)],"derivedFrom":[makeQuery(id+"F7.boolean.opBoolean","SPLIT",FACE,{"disambiguationData":[TD([makeQuery(id+"F3.opExtrude","CAP_FACE",FACE,{"disambiguationData":[OSD([sQuery(id+"F2.wireOp",EDGE,"E1.bottom"),sQuery(id+"F2.wireOp",EDGE,"E1.top"),sQuery(id+"F2.wireOp",EDGE,"E1.left"),sQuery(id+"F2.wireOp",EDGE,"E1.right")])],"isStart":true})])],"derivedFrom":subQ0}),makeQuery(id+"F9.opExtrude","SWEPT_FACE",FACE,{"disambiguationData":[OSD([sQuery(id+"F8.wireOp",EDGE,"E7.1.1.0")])]})]});}
            var Q44;
            Q44=makeQuery(id+"F7.boolean.opBoolean","INTERSECT",EDGE,{"disambiguationData":[OD(2.0)],"derivedFrom":[makeQuery(id+"F5.boolean.opBoolean","COPY",FACE,{"derivedFrom":makeQuery(id+"F5.opExtrude","SWEPT_FACE",FACE,{"disambiguationData":[OSD([sQuery(id+"F4.wireOp",EDGE,"E3.2.1.0")])]})}),makeQuery(id+"F7.opExtrude","SWEPT_FACE",FACE,{"disambiguationData":[OSD([sQuery(id+"F6.wireOp",EDGE,"E5.2.1.0")])]})]});
            var Q45;
            Q45=makeQuery(id+"F9.boolean.opBoolean","INTERSECT",EDGE,{"disambiguationData":[OD(0.0)],"derivedFrom":[makeQuery(id+"F7.boolean.opBoolean","COPY",FACE,{"disambiguationData":[OD(1.0)],"derivedFrom":makeQuery(id+"F7.opExtrude","SWEPT_FACE",FACE,{"disambiguationData":[OSD([sQuery(id+"F6.wireOp",EDGE,"E5.2.1.0")])]})}),makeQuery(id+"F9.opExtrude","SWEPT_FACE",FACE,{"disambiguationData":[OSD([sQuery(id+"F8.wireOp",EDGE,"E7.1.1.0")])]})]});
            var Q46;
            Q46=makeQuery(id+"F7.boolean.opBoolean","INTERSECT",EDGE,{"disambiguationData":[OD(0.0)],"derivedFrom":[makeQuery(id+"F5.boolean.opBoolean","COPY",FACE,{"derivedFrom":makeQuery(id+"F5.opExtrude","SWEPT_FACE",FACE,{"disambiguationData":[OSD([sQuery(id+"F4.wireOp",EDGE,"E3.2.1.0")])]})}),makeQuery(id+"F7.opExtrude","SWEPT_FACE",FACE,{"disambiguationData":[OSD([sQuery(id+"F6.wireOp",EDGE,"E5.2.1.0")])]})]});
            var Q47;
            {var subQ0=makeQuery(id+"F5.boolean.opBoolean","COPY",FACE,{"derivedFrom":makeQuery(id+"F5.opExtrude","SWEPT_FACE",FACE,{"disambiguationData":[OSD([sQuery(id+"F4.wireOp",EDGE,"E3.2.1.0")])]})});Q47=makeQuery(id+"F9.boolean.opBoolean","INTERSECT",EDGE,{"disambiguationData":[OD(1.0)],"derivedFrom":[makeQuery(id+"F7.boolean.opBoolean","SPLIT",FACE,{"disambiguationData":[TD([makeQuery(id+"F3.opExtrude","CAP_FACE",FACE,{"disambiguationData":[OSD([sQuery(id+"F2.wireOp",EDGE,"E1.bottom"),sQuery(id+"F2.wireOp",EDGE,"E1.top"),sQuery(id+"F2.wireOp",EDGE,"E1.left"),sQuery(id+"F2.wireOp",EDGE,"E1.right")])],"isStart":false})])],"derivedFrom":subQ0}),makeQuery(id+"F9.opExtrude","SWEPT_FACE",FACE,{"disambiguationData":[OSD([sQuery(id+"F8.wireOp",EDGE,"E7.1.1.0")])]})]});}
            var Q48;
            Q48=makeQuery(id+"F9.boolean.opBoolean","INTERSECT",EDGE,{"disambiguationData":[OD(1.0)],"derivedFrom":[makeQuery(id+"F7.boolean.opBoolean","COPY",FACE,{"disambiguationData":[OD(2.0)],"derivedFrom":makeQuery(id+"F7.opExtrude","SWEPT_FACE",FACE,{"disambiguationData":[OSD([sQuery(id+"F6.wireOp",EDGE,"E5.2.1.0")])]})}),makeQuery(id+"F9.opExtrude","SWEPT_FACE",FACE,{"disambiguationData":[OSD([sQuery(id+"F8.wireOp",EDGE,"E7.1.1.0")])]})]});
            var Q49;
            {var subQ0=makeQuery(id+"F5.boolean.opBoolean","COPY",FACE,{"derivedFrom":makeQuery(id+"F5.opExtrude","SWEPT_FACE",FACE,{"disambiguationData":[OSD([sQuery(id+"F4.wireOp",EDGE,"E3.2.1.0")])]})});Q49=makeQuery(id+"F9.boolean.opBoolean","INTERSECT",EDGE,{"disambiguationData":[OD(1.0)],"derivedFrom":[makeQuery(id+"F7.boolean.opBoolean","SPLIT",FACE,{"disambiguationData":[TD([makeQuery(id+"F3.opExtrude","CAP_FACE",FACE,{"disambiguationData":[OSD([sQuery(id+"F2.wireOp",EDGE,"E1.bottom"),sQuery(id+"F2.wireOp",EDGE,"E1.top"),sQuery(id+"F2.wireOp",EDGE,"E1.left"),sQuery(id+"F2.wireOp",EDGE,"E1.right")])],"isStart":true})])],"derivedFrom":subQ0}),makeQuery(id+"F9.opExtrude","SWEPT_FACE",FACE,{"disambiguationData":[OSD([sQuery(id+"F8.wireOp",EDGE,"E7.1.1.0")])]})]});}
            var Q50;
            {var subQ0=makeQuery(id+"F5.boolean.opBoolean","COPY",FACE,{"derivedFrom":makeQuery(id+"F5.opExtrude","SWEPT_FACE",FACE,{"disambiguationData":[OSD([sQuery(id+"F4.wireOp",EDGE,"E3.2.0.0")])]})});Q50=makeQuery(id+"F9.boolean.opBoolean","INTERSECT",EDGE,{"disambiguationData":[OD(1.0)],"derivedFrom":[makeQuery(id+"F7.boolean.opBoolean","SPLIT",FACE,{"disambiguationData":[TD([subQ0,makeQuery(id+"F7.opExtrude","SWEPT_FACE",FACE,{"disambiguationData":[OSD([sQuery(id+"F6.wireOp",EDGE,"E5.2.0.0")])]}),makeQuery(id+"F7.opExtrude","SWEPT_FACE",FACE,{"disambiguationData":[OSD([sQuery(id+"F6.wireOp",EDGE,"E5.2.1.0")])]})])],"derivedFrom":subQ0}),makeQuery(id+"F9.opExtrude","SWEPT_FACE",FACE,{"disambiguationData":[OSD([sQuery(id+"F8.wireOp",EDGE,"E7.0.1.0")])]})]});}
            var Q51;
            Q51=makeQuery(id+"F7.boolean.opBoolean","INTERSECT",EDGE,{"disambiguationData":[OD(2.0)],"derivedFrom":[makeQuery(id+"F5.boolean.opBoolean","COPY",FACE,{"derivedFrom":makeQuery(id+"F5.opExtrude","SWEPT_FACE",FACE,{"disambiguationData":[OSD([sQuery(id+"F4.wireOp",EDGE,"E3.2.0.0")])]})}),makeQuery(id+"F7.opExtrude","SWEPT_FACE",FACE,{"disambiguationData":[OSD([sQuery(id+"F6.wireOp",EDGE,"E5.2.1.0")])]})]});
            var Q52;
            {var subQ0=makeQuery(id+"F5.boolean.opBoolean","COPY",FACE,{"derivedFrom":makeQuery(id+"F5.opExtrude","SWEPT_FACE",FACE,{"disambiguationData":[OSD([sQuery(id+"F4.wireOp",EDGE,"E3.2.0.0")])]})});Q52=makeQuery(id+"F9.boolean.opBoolean","INTERSECT",EDGE,{"disambiguationData":[OD(0.0)],"derivedFrom":[makeQuery(id+"F7.boolean.opBoolean","SPLIT",FACE,{"disambiguationData":[TD([makeQuery(id+"F3.opExtrude","CAP_FACE",FACE,{"disambiguationData":[OSD([sQuery(id+"F2.wireOp",EDGE,"E1.bottom"),sQuery(id+"F2.wireOp",EDGE,"E1.top"),sQuery(id+"F2.wireOp",EDGE,"E1.left"),sQuery(id+"F2.wireOp",EDGE,"E1.right")])],"isStart":false}),subQ0,makeQuery(id+"F7.opExtrude","SWEPT_FACE",FACE,{"disambiguationData":[OSD([sQuery(id+"F6.wireOp",EDGE,"E5.2.1.0")])]})])],"derivedFrom":subQ0}),makeQuery(id+"F9.opExtrude","SWEPT_FACE",FACE,{"disambiguationData":[OSD([sQuery(id+"F8.wireOp",EDGE,"E7.0.1.0")])]})]});}
            var Q53;
            Q53=makeQuery(id+"F9.boolean.opBoolean","INTERSECT",EDGE,{"disambiguationData":[OD(0.0)],"derivedFrom":[makeQuery(id+"F7.boolean.opBoolean","COPY",FACE,{"disambiguationData":[OD(0.0)],"derivedFrom":makeQuery(id+"F7.opExtrude","SWEPT_FACE",FACE,{"disambiguationData":[OSD([sQuery(id+"F6.wireOp",EDGE,"E5.2.1.0")])]})}),makeQuery(id+"F9.opExtrude","SWEPT_FACE",FACE,{"disambiguationData":[OSD([sQuery(id+"F8.wireOp",EDGE,"E7.0.1.0")])]})]});
            var Q54;
            Q54=makeQuery(id+"F7.boolean.opBoolean","INTERSECT",EDGE,{"disambiguationData":[OD(1.0)],"derivedFrom":[makeQuery(id+"F5.boolean.opBoolean","COPY",FACE,{"derivedFrom":makeQuery(id+"F5.opExtrude","SWEPT_FACE",FACE,{"disambiguationData":[OSD([sQuery(id+"F4.wireOp",EDGE,"E3.2.0.0")])]})}),makeQuery(id+"F7.opExtrude","SWEPT_FACE",FACE,{"disambiguationData":[OSD([sQuery(id+"F6.wireOp",EDGE,"E5.2.1.0")])]})]});
            var Q55;
            Q55=makeQuery(id+"F9.boolean.opBoolean","INTERSECT",EDGE,{"disambiguationData":[OD(1.0)],"derivedFrom":[makeQuery(id+"F7.boolean.opBoolean","COPY",FACE,{"disambiguationData":[OD(2.0)],"derivedFrom":makeQuery(id+"F7.opExtrude","SWEPT_FACE",FACE,{"disambiguationData":[OSD([sQuery(id+"F6.wireOp",EDGE,"E5.2.1.0")])]})}),makeQuery(id+"F9.opExtrude","SWEPT_FACE",FACE,{"disambiguationData":[OSD([sQuery(id+"F8.wireOp",EDGE,"E7.0.1.0")])]})]});
            var Q56;
            Q56=makeQuery(id+"F7.boolean.opBoolean","INTERSECT",EDGE,{"disambiguationData":[OD(3.0)],"derivedFrom":[makeQuery(id+"F5.boolean.opBoolean","COPY",FACE,{"derivedFrom":makeQuery(id+"F5.opExtrude","SWEPT_FACE",FACE,{"disambiguationData":[OSD([sQuery(id+"F4.wireOp",EDGE,"E3.2.0.0")])]})}),makeQuery(id+"F7.opExtrude","SWEPT_FACE",FACE,{"disambiguationData":[OSD([sQuery(id+"F6.wireOp",EDGE,"E5.2.1.0")])]})]});
            var Q57;
            Q57=makeQuery(id+"F9.boolean.opBoolean","INTERSECT",EDGE,{"disambiguationData":[OD(0.0)],"derivedFrom":[makeQuery(id+"F7.boolean.opBoolean","COPY",FACE,{"disambiguationData":[OD(2.0)],"derivedFrom":makeQuery(id+"F7.opExtrude","SWEPT_FACE",FACE,{"disambiguationData":[OSD([sQuery(id+"F6.wireOp",EDGE,"E5.2.1.0")])]})}),makeQuery(id+"F9.opExtrude","SWEPT_FACE",FACE,{"disambiguationData":[OSD([sQuery(id+"F8.wireOp",EDGE,"E7.0.1.0")])]})]});
            var Q58;
            {var subQ0=makeQuery(id+"F5.boolean.opBoolean","COPY",FACE,{"derivedFrom":makeQuery(id+"F5.opExtrude","SWEPT_FACE",FACE,{"disambiguationData":[OSD([sQuery(id+"F4.wireOp",EDGE,"E3.2.0.0")])]})});Q58=makeQuery(id+"F9.boolean.opBoolean","INTERSECT",EDGE,{"disambiguationData":[OD(0.0)],"derivedFrom":[makeQuery(id+"F7.boolean.opBoolean","SPLIT",FACE,{"disambiguationData":[TD([subQ0,makeQuery(id+"F7.opExtrude","SWEPT_FACE",FACE,{"disambiguationData":[OSD([sQuery(id+"F6.wireOp",EDGE,"E5.2.0.0")])]}),makeQuery(id+"F7.opExtrude","SWEPT_FACE",FACE,{"disambiguationData":[OSD([sQuery(id+"F6.wireOp",EDGE,"E5.2.1.0")])]})])],"derivedFrom":subQ0}),makeQuery(id+"F9.opExtrude","SWEPT_FACE",FACE,{"disambiguationData":[OSD([sQuery(id+"F8.wireOp",EDGE,"E7.0.1.0")])]})]});}
            var Q59;
            Q59=makeQuery(id+"F9.boolean.opBoolean","INTERSECT",EDGE,{"disambiguationData":[OD(1.0)],"derivedFrom":[makeQuery(id+"F7.boolean.opBoolean","COPY",FACE,{"disambiguationData":[OD(1.0)],"derivedFrom":makeQuery(id+"F7.opExtrude","SWEPT_FACE",FACE,{"disambiguationData":[OSD([sQuery(id+"F6.wireOp",EDGE,"E5.2.1.0")])]})}),makeQuery(id+"F9.opExtrude","SWEPT_FACE",FACE,{"disambiguationData":[OSD([sQuery(id+"F8.wireOp",EDGE,"E7.1.1.0")])]})]});
            fillet(context, id + "F13", {"entities" : qUnion([Q0, Q1, Q2, Q3, Q4, Q5, Q6, Q7, Q8, Q9, Q10, Q11, Q12, Q13, Q14, Q15, Q16, Q17, Q18, Q19, Q20, Q21, Q22, Q23, Q24, Q25, Q26, Q27, Q28, Q29, Q30, Q31, Q32, Q33, Q34, Q35, Q36, Q37, Q38, Q39, Q40, Q41, Q42, Q43, Q44, Q45, Q46, Q47, Q48, Q49, Q50, Q51, Q52, Q53, Q54, Q55, Q56, Q57, Q58, Q59]), "radius" : 2.54 * mm, "tangentPropagation" : true, "allowEdgeOverflow" : false});
        }
    });
